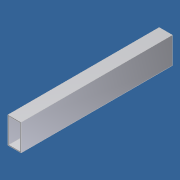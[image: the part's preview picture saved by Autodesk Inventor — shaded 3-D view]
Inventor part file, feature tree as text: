
AUTODESK INVENTOR PART (.ipt)
format: ipt  version: 2012 (Build 160160000, 160)  size: 73,216 bytes
history: native  units: in
note: dims shown in document units (in); Inventor stores cm internally (conversion verified against a paired STEP export)
features: extrude x1, sketch x1
ambient origin geometry x8: Origin, YZ Plane, XZ Plane, XY Plane, X Axis, Y Axis, Z Axis, Center Point
bodies: Solid1 (feature_tree)
feature tree (2):
  extrude  "Extrusion1"  Depth=3.5in
  sketch  "Sketch1"  dims[d0=1.75in d1=3.5in d2=0.125in d3=20.0in d4=0.0in]
